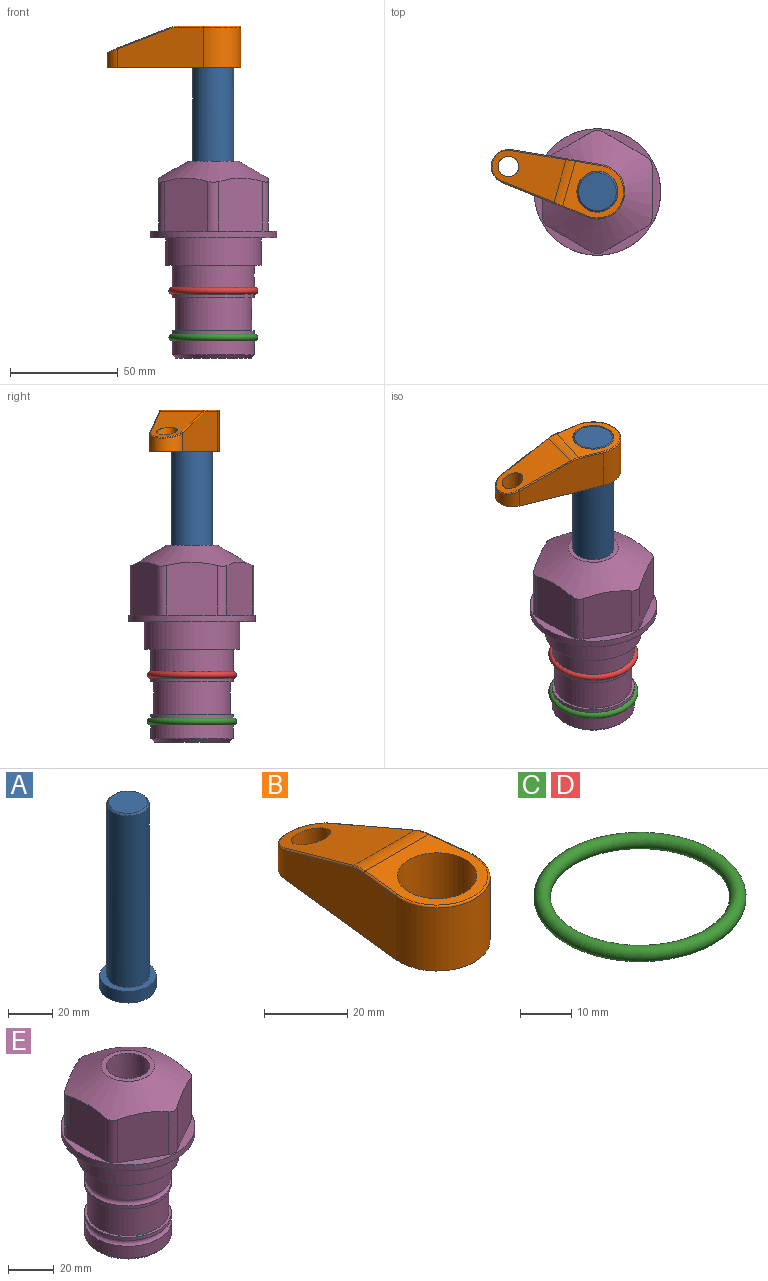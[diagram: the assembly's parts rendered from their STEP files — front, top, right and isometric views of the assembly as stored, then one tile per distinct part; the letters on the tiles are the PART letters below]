
ASSEMBLY  parts=5 mates=3
PART A: 6 faces, bbox 25.4x25.4x101.6 mm
  f0: plane 17.46x17.46mm, normal (0,0,1), area 239.5mm2, adj f5
  f1: plane 25.4x25.4mm, normal (0,0,-1), area 506.7mm2, adj f2
  f2: cylinder r=12.7mm len=25.4mm, axis (0,0,1), area 506.7mm2, adj f1,f3
  f3: plane 25.4x25.4mm, normal (0,0,1), area 221.7mm2, adj f2,f4
  f4: cylinder r=9.53mm len=94.46mm, axis (0,0,1), area 5653mm2, adj f3,f5
  f5: cone r=8.73mm half-angle=45deg, axis (0,0,-1), area 64.4mm2, adj f0,f4
PART B: 44 faces, bbox 27.5x64.5x19.1 mm
  f0: plane 2.3x0.95mm, normal (0,0,-1), area 1mm2, adj f25,f30,f34
  f1: plane 63.5x25.4mm, normal (0,0,-1), area 561.7mm2, adj f2,f3,f4,f5,f6,f7,f19,f20
  f2: cylinder r=12.7mm len=25.4mm, axis (0,0,-1), area 792.2mm2, adj f1,f3,f5,f13
  f3: plane 42.33x18.54mm, normal (0.99,0.11,0), area 647mm2, adj f1,f2,f4,f11,f12,f14
  f4: cylinder r=7.94mm len=15.78mm, axis (0,0,-1), area 158.6mm2, adj f1,f3,f5,f16
  f5: plane 42.33x18.54mm, normal (-0.99,0.11,0), area 647mm2, adj f1,f2,f4,f15,f17,f18
  f6: cylinder r=9.53mm len=19.05mm, axis (0,0,-1), area 1140.1mm2, adj f1,f8
  f7: cylinder r=4.76mm len=10.98mm, axis (0,0,-1), area 276.1mm2, adj f1,f9
  f8: plane 25.83x24.38mm, normal (0,0,1), area 262.2mm2, adj f6,f10,f11,f13,f15
  f9: plane 32.49x20.55mm, normal (0,0.34,0.94), area 489.9mm2, adj f7,f10,f14,f16,f18
  f10: cylinder r=12.7mm len=21.49mm, axis (-1,0,0), area 93.2mm2, adj f8,f9,f12,f17
  f11: cylinder r=0.51mm len=12.34mm, axis (0.11,-0.99,0), area 9.9mm2, adj f3,f8,f12,f13
  f12: bspline ~7.62x1.64mm, area 3.5mm2, adj f3,f10,f11,f14
  f13: torus R=12.19mm, axis (0,0,1), area 33.6mm2, adj f2,f8,f11,f15
  f14: cylinder r=0.51mm len=26.01mm, axis (0.1,-0.93,0.34), area 21.6mm2, adj f3,f9,f12,f16
  f15: cylinder r=0.51mm len=12.34mm, axis (0.11,0.99,0), area 9.9mm2, adj f5,f8,f13,f17
  f16: bspline ~15.78x7.05mm, area 15.7mm2, adj f4,f9,f14,f18
  f17: bspline ~7.62x1.64mm, area 3.5mm2, adj f5,f10,f15,f18
  f18: cylinder r=0.51mm len=26.01mm, axis (0.1,0.93,-0.34), area 21.6mm2, adj f5,f9,f16,f17
  f19: plane 21.6x14.29mm, normal (-0.99,-0.11,0), area 242.6mm2, adj f1,f26,f28,f34,f36,f38
  f20: plane 21.6x14.29mm, normal (0.99,-0.11,0), area 242.6mm2, adj f1,f27,f29,f37,f39,f41
  f21: cylinder r=12.7mm len=14.29mm, axis (0,0,-1), area 173.2mm2, adj f1,f26,f27,f30,f31,f33
  f22: cylinder r=7.94mm len=7.63mm, axis (0,0,-1), area 53.8mm2, adj f1,f28,f29,f42
  f23: plane 2.3x0.95mm, normal (0,0,-1), area 1mm2, adj f25,f33,f37
  f24: plane 17.94x12.32mm, normal (0,-0.34,-0.94), area 191.2mm2, adj f25,f38,f41,f42
  f25: cylinder r=9.53mm len=12.93mm, axis (-1,0,0), area 37.5mm2, adj f0,f23,f24,f31,f36,f39
  f26: cylinder r=1.59mm len=14.29mm, axis (0,0,-1), area 49mm2, adj f1,f19,f21,f32
  f27: cylinder r=1.59mm len=14.29mm, axis (0,0,-1), area 49mm2, adj f1,f20,f21,f35
  f28: cylinder r=1.59mm len=7.28mm, axis (0,0,-1), area 22.1mm2, adj f1,f19,f22,f40
  f29: cylinder r=1.59mm len=7.28mm, axis (0,0,-1), area 22.1mm2, adj f1,f20,f22,f43
  f30: torus R=14.29mm, axis (0,0,1), area 5.8mm2, adj f0,f21,f31,f32
  f31: bspline ~11.06x2.73mm, area 20.8mm2, adj f21,f25,f30,f33
  f32: sphere r=1.59mm, area 5.4mm2, adj f26,f30,f34
  f33: torus R=14.29mm, axis (0,0,1), area 5.8mm2, adj f21,f23,f31,f35
  f34: cylinder r=1.59mm len=1.68mm, axis (-0.11,0.99,0), area 2.4mm2, adj f0,f19,f32,f36
  f35: sphere r=1.59mm, area 5.4mm2, adj f27,f33,f37
  f36: bspline ~5.82x2.33mm, area 7.7mm2, adj f19,f25,f34,f38
  f37: cylinder r=1.59mm len=1.68mm, axis (0.11,0.99,0), area 2.4mm2, adj f20,f23,f35,f39
  f38: cylinder r=1.59mm len=18.33mm, axis (0.1,-0.93,0.34), area 46.7mm2, adj f19,f24,f36,f40
  f39: bspline ~5.82x2.33mm, area 7.7mm2, adj f20,f25,f37,f41
  f40: sphere r=1.59mm, area 3.6mm2, adj f28,f38,f42
  f41: cylinder r=1.59mm len=18.33mm, axis (0.1,0.93,-0.34), area 46.7mm2, adj f20,f24,f39,f43
  f42: bspline ~8.31x1.84mm, area 15.3mm2, adj f22,f24,f40,f43
  f43: sphere r=1.59mm, area 3.6mm2, adj f29,f41,f42
PART C: 1 faces, bbox 44.7x44.7x3.2 mm
  f0: torus R=19.05mm, axis (0,0,1), area 1193.9mm2
PART D: same geometry as C
PART E: 36 faces, bbox 58.7x58.7x91.2 mm
  f0: cylinder r=17.78mm len=35.56mm, axis (0,0,1), area 1670.8mm2, adj f23,f24,f31
  f1: cylinder r=19.05mm len=38.1mm, axis (0,0,1), area 1191.9mm2, adj f26,f27,f30
  f2: plane 58.66x58.66mm, normal (0,0,-1), area 1150.6mm2, adj f3,f28
  f3: cylinder r=29.33mm len=58.66mm, axis (0,0,-1), area 585.1mm2, adj f2,f4
  f4: plane 58.66x58.66mm, normal (0,0,1), area 475.9mm2, adj f3,f5,f6,f7,f8,f9,f10,f11
  f5: plane 24.5x20.32mm, normal (0.5,-0.87,0), area 562.8mm2, adj f4,f15,f16,f17
  f6: plane 24.5x20.32mm, normal (-0.5,-0.87,0), area 562.8mm2, adj f4,f14,f15,f17
  f7: plane 24.5x23.48mm, normal (-1,0,0), area 562.8mm2, adj f4,f13,f14,f17
  f8: plane 24.5x20.32mm, normal (-0.5,0.87,0), area 562.8mm2, adj f4,f12,f13,f17
  f9: plane 24.5x20.32mm, normal (0.5,0.87,0), area 562.8mm2, adj f4,f11,f12,f17
  f10: plane 24.5x23.48mm, normal (1,0,0), area 562.8mm2, adj f4,f11,f16,f17
  f11: cylinder r=5.08mm len=23.01mm, axis (0,0,-1), area 121.2mm2, adj f4,f9,f10,f17
  f12: cylinder r=5.08mm len=23.01mm, axis (0,0,-1), area 121.2mm2, adj f4,f8,f9,f17
  f13: cylinder r=5.08mm len=23.01mm, axis (0,0,-1), area 121.2mm2, adj f4,f7,f8,f17
  f14: cylinder r=5.08mm len=23.01mm, axis (0,0,-1), area 121.2mm2, adj f4,f6,f7,f17
  f15: cylinder r=5.08mm len=23.01mm, axis (0,0,-1), area 121.2mm2, adj f4,f5,f6,f17
  f16: cylinder r=5.08mm len=23.01mm, axis (0,0,-1), area 121.2mm2, adj f4,f5,f10,f17
  f17: cone r=11.73mm half-angle=60deg, axis (0,0,-1), area 2071.8mm2, adj f5,f6,f7,f8,f9,f10,f11,f12
  f18: plane 23.46x23.46mm, normal (0,0,1), area 147.4mm2, adj f17,f35
  f19: plane 34.93x34.93mm, normal (0,0,-1), area 958mm2, adj f29
  f20: cylinder r=19.05mm len=38.1mm, axis (0,0,1), area 760.1mm2, adj f21,f29
  f21: torus R=19.05mm, axis (0,0,1), area 565.3mm2, adj f20,f22
  f22: cylinder r=19.05mm len=38.1mm, axis (0,0,1), area 190mm2, adj f21,f23
  f23: plane 38.1x38.1mm, normal (0,0,1), area 146.9mm2, adj f0,f22
  f24: plane 38.1x38.1mm, normal (0,0,-1), area 146.9mm2, adj f0,f25
  f25: cylinder r=19.05mm len=38.1mm, axis (0,0,1), area 190mm2, adj f24,f26
  f26: torus R=19.05mm, axis (0,0,1), area 565.3mm2, adj f1,f25
  f27: plane 44.45x44.45mm, normal (0,0,-1), area 411.7mm2, adj f1,f28
  f28: cylinder r=22.23mm len=44.45mm, axis (0,0,1), area 1773.5mm2, adj f2,f27
  f29: cone r=19.05mm half-angle=45deg, axis (0,0,1), area 257.5mm2, adj f19,f20
  f30: cylinder r=3.17mm len=6.75mm, axis (-1,0,0), area 128mm2, adj f1,f33
  f31: cylinder r=3.17mm len=6.35mm, axis (-1,0,0), area 102.5mm2, adj f0,f33
  f32: plane 25.4x25.4mm, normal (0,0,1), area 506.7mm2, adj f33
  f33: cylinder r=12.7mm len=66.42mm, axis (0,0,-1), area 5236.2mm2, adj f30,f31,f32,f34
  f34: cone r=9.53mm half-angle=30deg, axis (0,0,-1), area 443.4mm2, adj f33,f35
  f35: cylinder r=9.53mm len=19.05mm, axis (0,0,-1), area 849mm2, adj f18,f34
PLACE A rot(axis=(0,0,1),164.2deg) t=(0,0,24.57)mm
PLACE B rot(axis=(0,0,1),74.2deg) t=(0,0,79.18)mm fixed
PLACE C t=(0,0,-21.59)mm
PLACE D at identity
PLACE E at identity fixed
MATE fastened C.f0 <-> E.f0  axis (0,0,1) through (0,0,-46.1)mm
MATE cylindrical A.f2 <-> E.f0  axis (0,0,1) through (0,0,50.2)mm
MATE fastened B.f2 <-> A.f2  axis (0,0,1) through (0,0,98.23)mm
